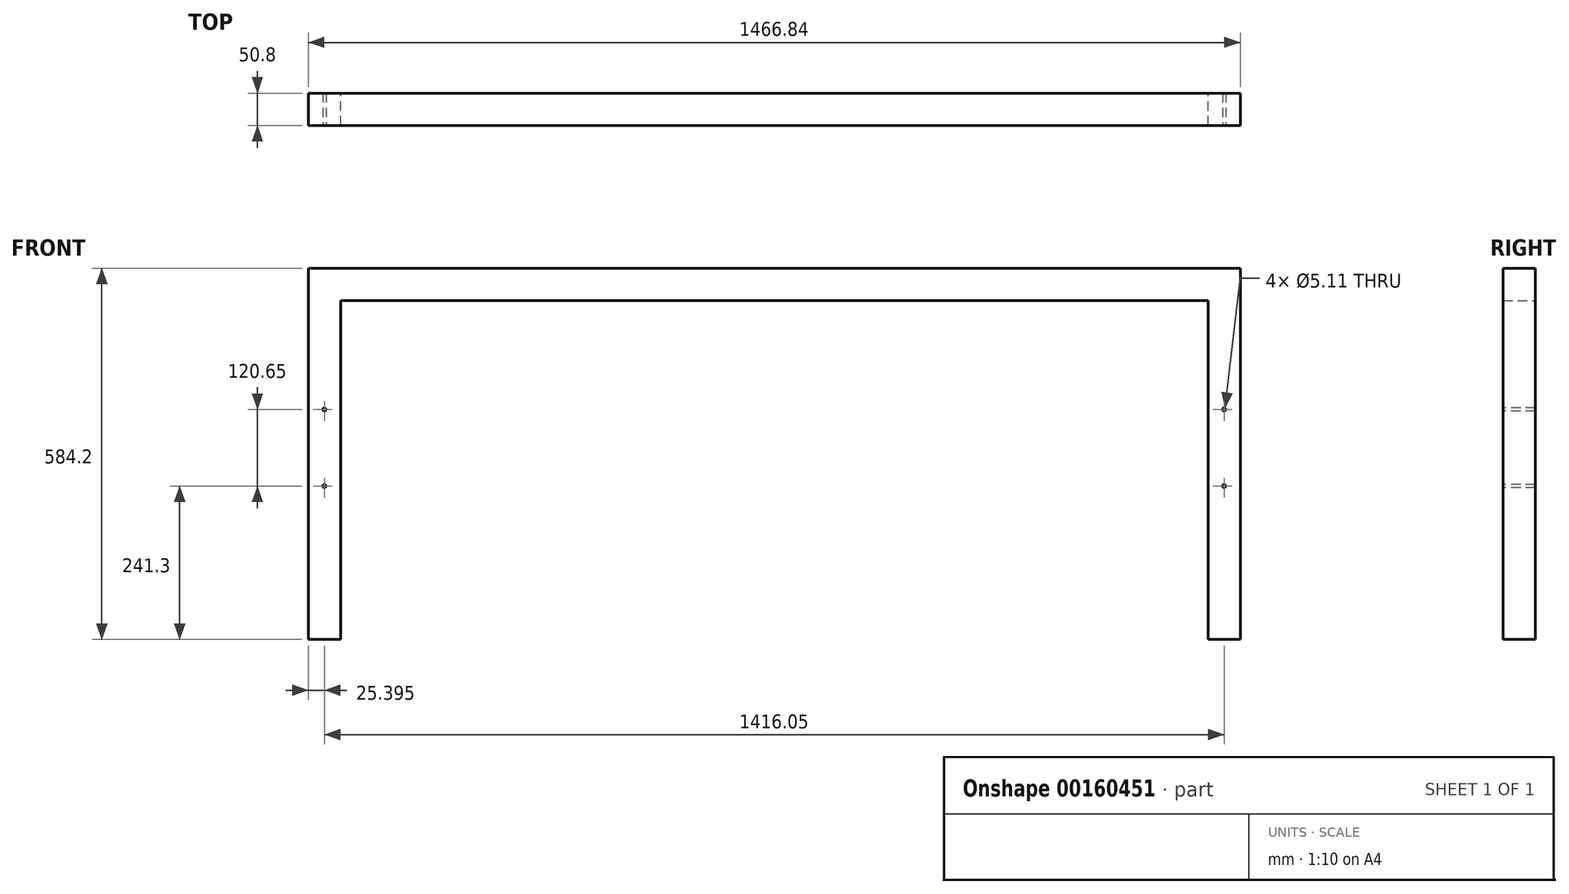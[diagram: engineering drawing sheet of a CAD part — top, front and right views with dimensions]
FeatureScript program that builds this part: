
annotation { "Feature Type Name" : "Feature", "Feature Type Description" : "" }
export const myFeature = defineFeature(function(context is Context, id is Id, definition is map)
    precondition{}
    {
        {
            var Q0;
            Q0=qCreatedBy(makeId("Front.planeOp"),FACE);
            var sketch = newSketch(context, id + "F0", { "sketchPlane" : qUnion([Q0])});
            skLineSegment(sketch, "E0.bottom", {"start": v(-733.43, 292.1) * mm, "end": v(733.43, 292.1) * mm});
            skLineSegment(sketch, "E0.top", {"start": v(-733.43, -292.1) * mm, "end": v(-682.62, -292.1) * mm});
            skLineSegment(sketch, "E0.left", {"start": v(-733.43, 292.1) * mm, "end": v(-733.43, -292.1) * mm});
            skLineSegment(sketch, "E0.right", {"start": v(733.43, 292.1) * mm, "end": v(733.42, -292.1) * mm});
            skPoint(sketch, "E0.middle", {"position": v(0, 0) * mm});
            skLineSegment(sketch, "E1.top", {"start": v(-682.62, 241.3) * mm, "end": v(682.62, 241.3) * mm});
            skLineSegment(sketch, "E1.left", {"start": v(-682.62, -292.1) * mm, "end": v(-682.62, 241.3) * mm});
            skLineSegment(sketch, "E1.right", {"start": v(682.62, -292.1) * mm, "end": v(682.62, 241.3) * mm});
            skPoint(sketch, "E2", {"position": v(0, 241.3) * mm});
            skLineSegment(sketch, "E3.trimOffspring", {"start": v(682.62, -292.1) * mm, "end": v(733.42, -292.1) * mm});
            skSolve(sketch);
        }
        {
            var Q0;
            Q0=makeQuery(id+"F0.imprint","IMPRINT",FACE,{"disambiguationData":[TD([[makeQuery(id+"F0.imprint","IMPRINT",EDGE,{"derivedFrom":sQuery(id+"F0.wireOp",EDGE,"E0.bottom")}),-1.0]])]});
            extrude(context, id + "F1", {"entities" : qUnion([Q0]), "depth" : 25.4 * mm, "hasSecondDirection" : true, "secondDirectionOppositeDirection" : true, "secondDirectionDepth" : 25.4 * mm});
        }
        {
            var Q0;
            Q0=makeQuery(id+"F1.opExtrude","CAP_FACE",FACE,{"disambiguationData":[OSD([sQuery(id+"F0.wireOp",EDGE,"E0.bottom"),sQuery(id+"F0.wireOp",EDGE,"E0.top"),sQuery(id+"F0.wireOp",EDGE,"E0.left"),sQuery(id+"F0.wireOp",EDGE,"E0.right"),sQuery(id+"F0.wireOp",EDGE,"E1.top"),sQuery(id+"F0.wireOp",EDGE,"E1.left"),sQuery(id+"F0.wireOp",EDGE,"E1.right"),sQuery(id+"F0.wireOp",EDGE,"E3.trimOffspring")])],"isStart":false});
            var sketch = newSketch(context, id + "F2", { "sketchPlane" : qUnion([Q0])});
            skLineSegment(sketch, "E4", {"start": v(-708.03, -292.1) * mm, "end": v(-708.03, 292.1) * mm, "construction": true});
            skLineSegment(sketch, "E5", {"start": v(708.02, -292.1) * mm, "end": v(708.02, 292.1) * mm, "construction": true});
            skPoint(sketch, "E6", {"position": v(-708.03, -50.8) * mm});
            skPoint(sketch, "E7", {"position": v(-708.03, 69.85) * mm});
            skPoint(sketch, "E8", {"position": v(708.02, 69.85) * mm});
            skPoint(sketch, "E9", {"position": v(708.02, -50.8) * mm});
            skSolve(sketch);
        }
        {
            var Q0;
            Q0=sQuery(id+"F2.wireOp",VERTEX,"E6");
            var Q1;
            Q1=sQuery(id+"F2.wireOp",VERTEX,"E9");
            var Q2;
            Q2=sQuery(id+"F2.wireOp",VERTEX,"E8");
            var Q3;
            Q3=sQuery(id+"F2.wireOp",VERTEX,"E7");
            var Q4;
            Q4=makeQuery(id+"F1.opExtrude","SWEPT_BODY",BODY,{"disambiguationData":[OSD([sQuery(id+"F0.wireOp",EDGE,"E0.bottom"),sQuery(id+"F0.wireOp",EDGE,"E0.top"),sQuery(id+"F0.wireOp",EDGE,"E0.left"),sQuery(id+"F0.wireOp",EDGE,"E0.right"),sQuery(id+"F0.wireOp",EDGE,"E1.top"),sQuery(id+"F0.wireOp",EDGE,"E1.left"),sQuery(id+"F0.wireOp",EDGE,"E1.right"),sQuery(id+"F0.wireOp",EDGE,"E3.trimOffspring")])]});
            hole(context, id + "F3", {"style" : HoleStyle.SIMPLE, "endStyle" : HoleEndStyle.THROUGH, "standardTappedOrClearance" : lookupTablePath({ "standard" : "ANSI", "engagement" : "75%", "pitch" : "20 tpi", "size" : "1/4", "type" : "Tapped" }), "standardBlindInLast" : lookupTablePath({ "standard" : "ANSI", "engagement" : "75%", "pitch" : "20 tpi", "size" : "1/4", "type" : "Tapped" }), "holeDiameter" : 5.1 * mm, "locations" : qUnion([Q0, Q1, Q2, Q3]), "scope" : qUnion([Q4]), "isTappedThrough" : true, "majorDiameter" : 6.35 * mm, "showTappedDepth" : true});
        }
    });
